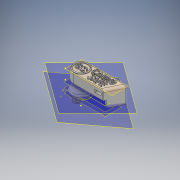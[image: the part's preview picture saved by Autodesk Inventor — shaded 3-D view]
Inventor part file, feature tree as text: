
AUTODESK INVENTOR PART (.ipt)
format: ipt  version: 2017 (Build 210142000, 142)  size: 1,229,824 bytes
history: native  units: mm
features: sketch x33, extrude x15, fillet x15, plane x8, loft x3, chamfer x2, other x2, projected_geometry x1
ambient origin geometry x8: Origin, YZ Plane, XZ Plane, XY Plane, X Axis, Y Axis, Z Axis, Center Point
bodies: Solid1 (feature_tree)
feature tree (79):
  sketch  "Sketch1"  dims[d0=40.0mm d1=14.0mm]
  extrude  "Extrusion1"  Depth=14.0mm
  extrude  "Extrusion2"  Depth=8.5mm TaperAngle=0.0deg
  fillet  "Fillet1"  Radius=8.5mm
  extrude  "Extrusion3"  Depth=7.0mm
  fillet  "Fillet2"  Radius=6.0mm
  fillet  "Fillet3"  Radius=2.0mm
  fillet  "Fillet4"  Radius=0.5mm
  fillet  "Fillet5"  Radius=0.5mm
  sketch  "Sketch5"  dims[d17=2.3mm d18=8.4mm]
  sketch  "Sketch6"  dims[d19=4.7mm d20=17.6mm d21=3.5mm d22=13.9mm d23=0.0mm d24=90.0deg]
  plane  "Work Plane1"
  sketch  "Sketch7"  dims[d25=0.0mm d26=90.0deg d27=0.0mm d28=90.0deg]
  plane  "Work Plane2"
  sketch  "Sketch8"  dims[d29=0.0mm d30=90.0deg d31=0.0mm d32=90.0deg]
  plane  "Work Plane3"
  sketch  "Sketch9"  dims[d33=0.0mm d34=90.0deg d35=2.0mm d36=2.0mm d37=1.0mm d39=2.094395mm d41=4.0mm d42=0.0mm]
  loft  "Loft1"
  loft  "Loft2"
  loft  "Loft3"
  fillet  "Fillet6"  Radius=3.5mm
  fillet  "Fillet7"  Radius=13.9mm
  fillet  "Fillet8"  [1 undecoded]
  sketch  "Sketch10"  dims[d43=0.0mm d44=5.0mm d45=2.5mm d46=0.0mm]
  plane  "Work Plane4"
  sketch  "Sketch11"  dims[d47=0.0mm d48=6.1mm]
  sketch  "Sketch12"  dims[d49=2.5mm d50=0.0mm d51=3.05mm]
  extrude  "Extrusion4"  TaperAngle=0.0deg  [1 undecoded]
  plane  "Work Plane5"
  plane  "Work Plane6"
  extrude  "Extrusion5"  TaperAngle=0.0deg  [1 undecoded]
  sketch  "Sketch15"  dims[d69=0.0mm d101=1.0mm d102=0.0mm]
  plane  "Work Plane7"
  extrude  "Extrusion6"  Depth=2.0mm
  fillet  "Fillet9"  Radius=2.0mm
  fillet  "Fillet10"  Radius=1.0mm
  fillet  "Fillet11"  Radius=2.094395mm
  fillet  "Fillet12"  Radius=4.0mm
  sketch  "Sketch17"  dims[d106=0.1mm d107=0.1mm]
  extrude  "Extrusion7"  Depth=5.0mm
  chamfer  "Chamfer1"  Distance=2.5mm
  extrude  "Extrusion8"  Depth=6.1mm
  plane  "Work Plane8"
  sketch  "Sketch21"  dims[d122=0.5mm]
  sketch  "Sketch23"  dims[d123=0.2mm]
  sketch  "Sketch24"  dims[d124=6.6mm d125=0.0mm]
  extrude  "Extrusion9"  Depth=3.05mm
  extrude  "Extrusion10"  Depth=1.0mm
  fillet  "Fillet13"  Radius=1.0mm
  fillet  "Fillet14"  Radius=2.0mm
  fillet  "Fillet15"  Radius=1.5mm
  extrude  "Extrusion11"  Depth=0.5mm TaperAngle=0.0deg
  sketch  "Sketch26"  dims[d126=1.0mm d127=0.0mm]
  extrude  "Extrusion12"  Depth=1.0mm TaperAngle=0.0deg
  sketch  "Sketch28"
  sketch  "Sketch29"
  sketch  "Sketch30"
  extrude  "Extrusion13"  Depth=0.1mm
  sketch  "Sketch31"
  sketch  "Sketch32"
  sketch  "Sketch33"
  sketch  "Sketch34"
  sketch  "Sketch35"
  extrude  "Extrusion14"  Depth=0.1mm
  extrude  "Extrusion15"  Depth=1.0mm
  chamfer  "Chamfer2"  Distance=0.5mm
  sketch  "Sketch39"
  sketch  "Sketch2"  dims[d2=7.0mm d3=8.5mm d4=0.0mm d5=8.5mm d6=0.0mm]
  sketch  "Sketch3"  dims[d7=2.0mm d8=7.0mm d9=6.0mm d10=0.0mm d11=2.0mm d12=0.5mm d13=0.5mm]
  sketch  "Sketch4"  dims[d14=0.5mm d16=12.4mm]
  other  "Edges1"
  other  "Edges2"
  sketch  "Sketch13"  dims[d52=1.0mm d53=1.0mm d54=1.0mm d58=2.0mm d59=1.5mm d60=0.0mm]
  sketch  "Sketch14"  dims[d61=0.75mm d62=2.0mm d63=45.0deg d67=0.5mm d68=0.0mm]
  sketch  "Sketch16"  dims[d103=1.0mm d104=0.0mm d105=0.1mm]
  projected_geometry  "Projected Loop1"
  sketch  "Sketch19"  dims[d109=1.0mm d110=0.0mm d112=1.0mm d113=0.5mm d114=0.0mm]
  sketch  "Sketch20"  dims[d116=0.5mm d117=0.0mm]
  sketch  "Sketch27"  dims[d128=0.49mm d129=2.0mm d130=45.0deg]
note: 3 required parameter values undecoded (feature->parameter linkage not recoverable at this tier; creation-order binding heuristic only, values carry confidence <= 0.55)
